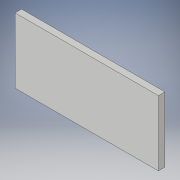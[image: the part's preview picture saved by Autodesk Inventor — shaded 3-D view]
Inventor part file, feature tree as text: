
AUTODESK INVENTOR PART (.ipt)
format: ipt  version: 2017 (Build 210142000, 142)  size: 86,528 bytes
history: native  units: in
note: dims shown in document units (in); Inventor stores cm internally (conversion verified against a paired STEP export)
features: extrude x1, sketch x1
ambient origin geometry x8: Origin, YZ Plane, XZ Plane, XY Plane, X Axis, Y Axis, Z Axis, Center Point
bodies: Solid1 (feature_tree)
feature tree (2):
  extrude  "Extrusion1"  Depth=11.0in
  sketch  "Sketch1"  dims[d0=5.0in d1=11.0in d2=0.5in d3=0.0in]
